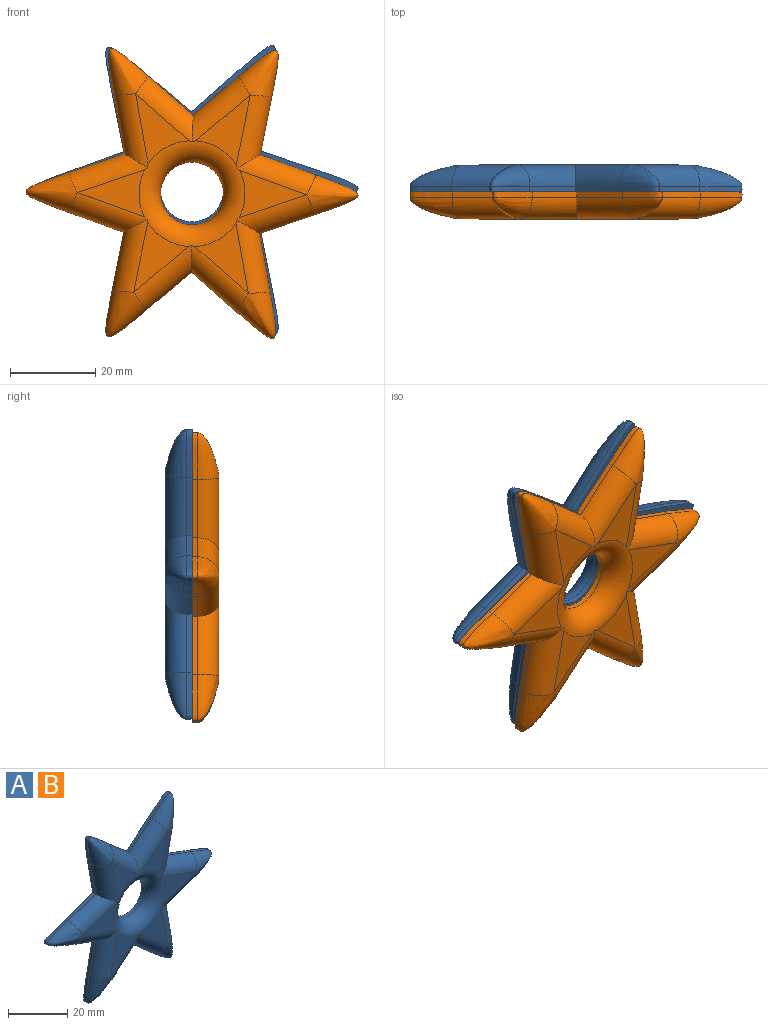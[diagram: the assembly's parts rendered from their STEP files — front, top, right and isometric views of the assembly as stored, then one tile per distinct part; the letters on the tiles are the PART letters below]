
ASSEMBLY  parts=2 mates=1
PART A: 45 faces, bbox 84.7x8.7x73.8 mm
  f0: plane 16.43x12.85mm, normal (0,-1,0), area 78mm2, adj f37,f40,f41
  f1: plane 15.87x11.09mm, normal (0,-1,0), area 78mm2, adj f40,f42,f43
  f2: plane 16.53x12.58mm, normal (0,-1,0), area 78mm2, adj f30,f39,f40
  f3: plane 16.43x12.85mm, normal (0,-1,0), area 78mm2, adj f31,f32,f40
  f4: plane 15.87x11.09mm, normal (0,-1,0), area 78mm2, adj f33,f34,f40
  f5: plane 13.68x2.74mm, normal (0.98,0,-0.2), area 17.7mm2, adj f6,f22,f25,f41
  f6: extruded ~10.93x9.45mm, area 28.2mm2, adj f5,f7,f25,f38
  f7: plane 10.7x9mm, normal (-0.64,0,0.77), area 17.7mm2, adj f6,f8,f25,f37
  f8: plane 10.48x9.21mm, normal (0.66,0,0.75), area 17.7mm2, adj f7,f9,f25,f36
  f9: extruded ~10.96x9.32mm, area 28.2mm2, adj f8,f10,f25,f28
  f10: plane 13.76x2.44mm, normal (-0.98,0,-0.17), area 17.7mm2, adj f9,f11,f25,f35
  f11: plane 13.22x4.47mm, normal (-0.32,0,0.95), area 17.7mm2, adj f10,f12,f25,f34
  f12: extruded ~9.92x9.24mm, area 28.2mm2, adj f11,f13,f25,f27
  f13: plane 13.14x4.76mm, normal (-0.34,0,-0.94), area 17.7mm2, adj f12,f14,f25,f33
  f14: plane 13.68x2.74mm, normal (-0.98,0,0.2), area 17.7mm2, adj f13,f15,f25,f32
  f15: extruded ~10.93x9.45mm, area 28.2mm2, adj f14,f16,f25,f26
  f16: plane 10.7x9mm, normal (0.64,0,-0.77), area 17.7mm2, adj f15,f17,f25,f31
  f17: plane 10.48x9.21mm, normal (-0.66,0,-0.75), area 17.7mm2, adj f16,f18,f25,f30
  f18: extruded ~10.96x9.32mm, area 28.2mm2, adj f17,f19,f25,f29
  f19: plane 13.76x2.44mm, normal (0.98,0,0.17), area 17.7mm2, adj f18,f20,f25,f39
  f20: plane 13.22x4.47mm, normal (0.32,0,-0.95), area 17.7mm2, adj f19,f21,f25,f42
  f21: extruded ~9.92x9.24mm, area 28.2mm2, adj f20,f22,f25,f44
  f22: plane 13.14x4.76mm, normal (0.34,0,0.94), area 17.7mm2, adj f5,f21,f25,f43
  f23: cylinder r=7.39mm len=14.78mm, axis (0,1,0), area 59mm2, adj f25,f40
  f24: plane 16.53x12.58mm, normal (0,-1,0), area 78mm2, adj f35,f36,f40
  f25: plane 84.7x73.78mm, normal (0,1,0), area 2135.9mm2, adj f5,f6,f7,f8,f9,f10,f11,f12
  f26: bspline ~10.93x9.45mm, area 111mm2, adj f15,f31,f32
  f27: bspline ~12.07x9.24mm, area 111mm2, adj f12,f33,f34
  f28: bspline ~10.97x9.33mm, area 111mm2, adj f9,f35,f36
  f29: bspline ~10.97x9.33mm, area 111mm2, adj f18,f30,f39
  f30: cylinder r=5.08mm len=16.92mm, axis (-0.75,0,0.66), area 122.3mm2, adj f2,f17,f29,f31,f40
  f31: cylinder r=5.08mm len=17.11mm, axis (-0.77,0,-0.64), area 122mm2, adj f3,f16,f26,f30,f40
  f32: cylinder r=5.08mm len=18.71mm, axis (0.2,0,0.98), area 121.7mm2, adj f3,f14,f26,f33,f40
  f33: cylinder r=5.08mm len=18.73mm, axis (-0.94,0,0.34), area 122mm2, adj f4,f13,f27,f32,f40
  f34: cylinder r=5.08mm len=18.74mm, axis (0.95,0,0.32), area 121.7mm2, adj f4,f11,f27,f35,f40
  f35: cylinder r=5.08mm len=18.7mm, axis (-0.17,0,0.98), area 122mm2, adj f10,f24,f28,f34,f40
  f36: cylinder r=5.08mm len=16.92mm, axis (0.75,0,-0.66), area 121.7mm2, adj f8,f24,f28,f37,f40
  f37: cylinder r=5.08mm len=17.11mm, axis (0.77,0,0.64), area 122mm2, adj f0,f7,f36,f38,f40
  f38: bspline ~10.93x9.45mm, area 111mm2, adj f6,f37,f41
  f39: cylinder r=5.08mm len=18.7mm, axis (0.17,0,-0.98), area 122mm2, adj f2,f19,f29,f40,f42
  f40: torus R=12.47mm, axis (0,-1,0), area 461.6mm2, adj f0,f1,f2,f3,f4,f23,f24,f30
  f41: cylinder r=5.08mm len=18.71mm, axis (-0.2,0,-0.98), area 121.7mm2, adj f0,f5,f38,f40,f43
  f42: cylinder r=5.08mm len=18.74mm, axis (-0.95,0,-0.32), area 121.7mm2, adj f1,f20,f39,f40,f44
  f43: cylinder r=5.08mm len=18.73mm, axis (0.94,0,-0.34), area 122mm2, adj f1,f22,f40,f41,f44
  f44: bspline ~12.07x9.24mm, area 111mm2, adj f21,f42,f43
PART B: same geometry as A
PLACE A rot(axis=(1,0,0),180deg) t=(11.69,11.57,26.7)mm
PLACE B t=(11.69,11.57,25.91)mm
MATE fastened A.f25 <-> B.f25  axis (0,-1,0) through (-27.37,11.57,26.31)mm
